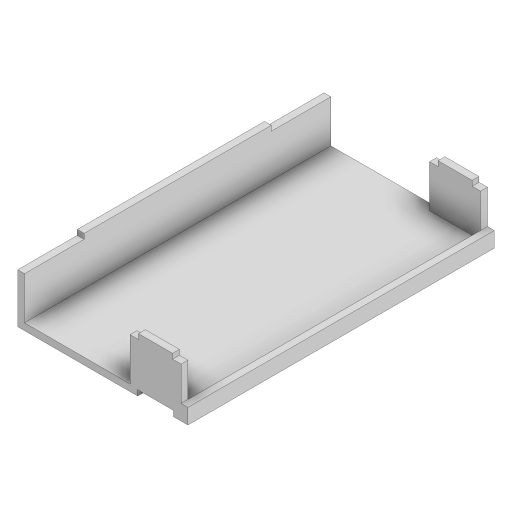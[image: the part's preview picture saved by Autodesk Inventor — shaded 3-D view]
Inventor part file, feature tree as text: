
AUTODESK INVENTOR PART (.ipt)
format: ipt  version: 2024 (Build 280153000, 153)  size: 226,816 bytes
history: native  units: mm
features: projected_geometry x6, extrude x5, sketch x5
ambient origin geometry x8: Origin, YZ Plane, XZ Plane, XY Plane, X Axis, Y Axis, Z Axis, Center Point
bodies: Solid1 (feature_tree)
feature tree (16):
  extrude  "Extrusion1"  Depth=180.0mm
  extrude  "Extrusion2"  Depth=4.0mm
  extrude  "Extrusion3"  Depth=5.0mm TaperAngle=0.0deg
  extrude  "Extrusion4"  Depth=4.0mm
  extrude  "Extrusion5"  Depth=4.0mm
  sketch  "Sketch1"  dims[d0=100.0mm d1=180.0mm]
  sketch  "Sketch2"  dims[d2=4.0mm d3=0.0mm d4=4.0mm]
  sketch  "Sketch3"  dims[d5=4.0mm d6=5.0mm d7=0.0mm]
  sketch  "Sketch4"  dims[d8=30.0mm d9=4.0mm]
  projected_geometry  "Projected Loop1"
  projected_geometry  "Projected Loop2"
  projected_geometry  "Projected Loop3"
  sketch  "Sketch5"  dims[d10=4.0mm d11=4.0mm d12=25.0mm d13=0.0mm d14=55.0mm d15=110.0mm d16=10.0mm d17=20.0mm d18=3.0mm d19=0.0mm d20=3.2mm d21=0.0mm d22=0.5mm d23=0.5mm d24=0.5mm d25=0.5mm d26=0.5mm d27=0.5mm]
  projected_geometry  "Projected Loop4"
  projected_geometry  "Projected Loop5"
  projected_geometry  "Projected Loop6"
